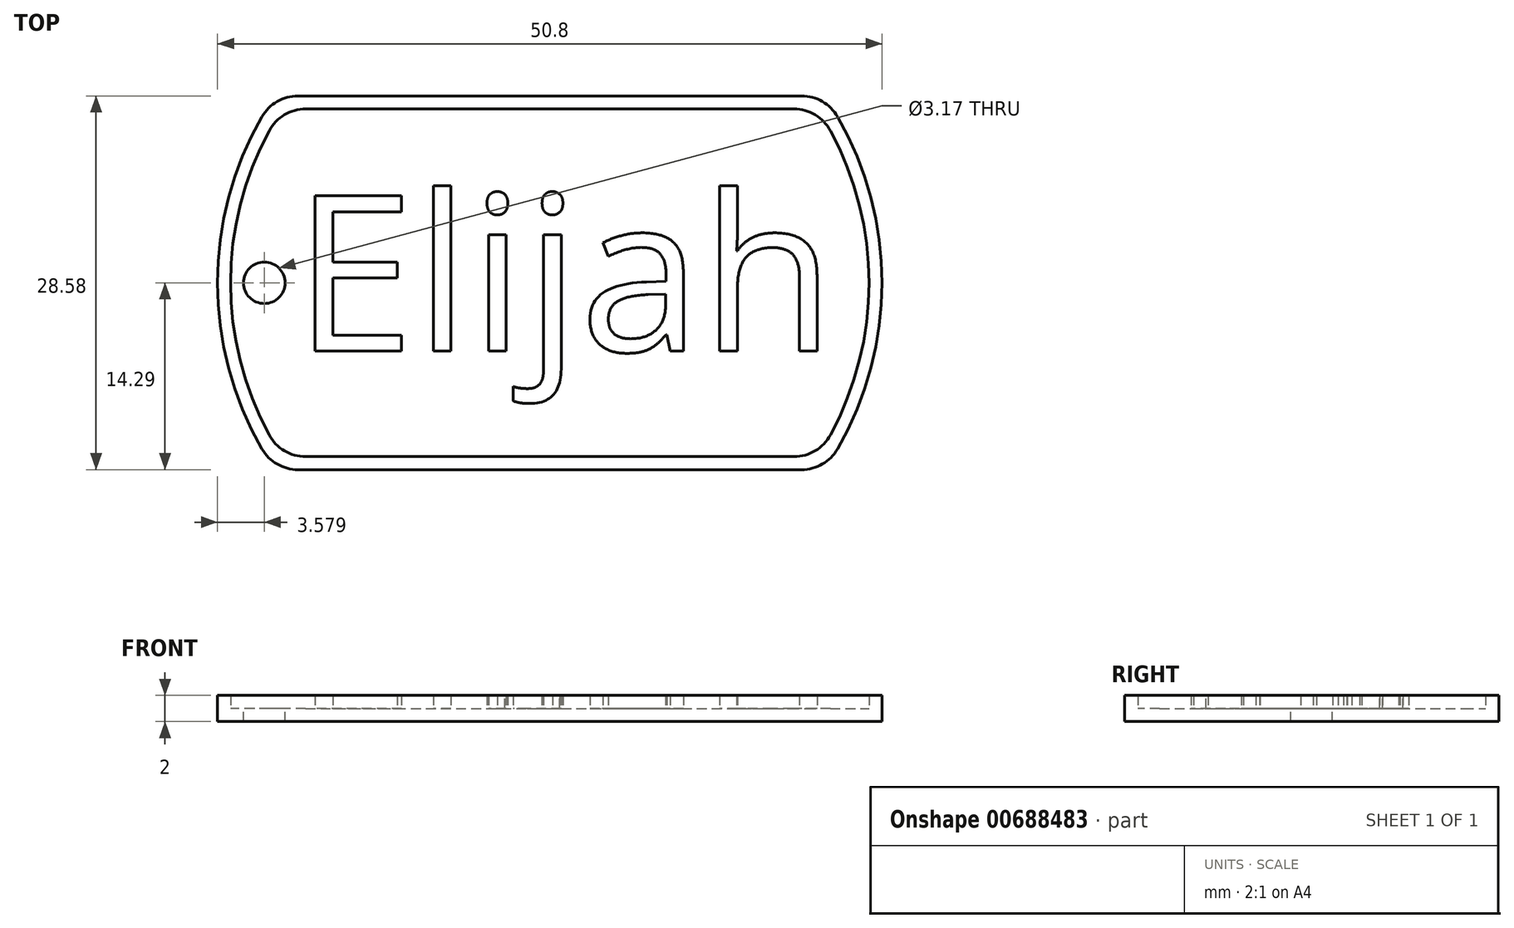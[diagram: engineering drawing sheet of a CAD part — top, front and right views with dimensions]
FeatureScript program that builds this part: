
annotation { "Feature Type Name" : "Feature", "Feature Type Description" : "" }
export const myFeature = defineFeature(function(context is Context, id is Id, definition is map)
    precondition{}
    {
        {
            var Q0;
            Q0=qCreatedBy(makeId("Top.planeOp"),FACE);
            var sketch = newSketch(context, id + "F0", { "sketchPlane" : qUnion([Q0])});
            skArc(sketch, "E0", {"start": v(-22, 12.7) * mm, "mid": v(-25.4, 0) * mm, "end": v(-22, -12.7) * mm});
            skLineSegment(sketch, "E1.top", {"start": v(-19.25, -14.29) * mm, "end": v(19.25, -14.29) * mm});
            skArc(sketch, "E2.trimOffspring", {"start": v(22, -12.7) * mm, "mid": v(25.4, 0) * mm, "end": v(22, 12.7) * mm});
            skLineSegment(sketch, "E3", {"start": v(-19.25, 14.29) * mm, "end": v(19.25, 14.29) * mm});
            skPoint(sketch, "E4.visualSharp", {"position": v(-21, 14.29) * mm});
            skArc(sketch, "E4.filletArc", {"start": v(-19.25, 14.29) * mm, "mid": v(-20.83, 13.86) * mm, "end": v(-22, 12.7) * mm});
            skPoint(sketch, "E5.visualSharp", {"position": v(21, 14.29) * mm});
            skArc(sketch, "E5.filletArc", {"start": v(22, 12.7) * mm, "mid": v(20.83, 13.86) * mm, "end": v(19.25, 14.29) * mm});
            skPoint(sketch, "E6.visualSharp", {"position": v(21, -14.29) * mm});
            skArc(sketch, "E6.filletArc", {"start": v(19.25, -14.29) * mm, "mid": v(20.83, -13.86) * mm, "end": v(22, -12.7) * mm});
            skPoint(sketch, "E7.visualSharp", {"position": v(-21, -14.29) * mm});
            skArc(sketch, "E7.filletArc", {"start": v(-22, -12.7) * mm, "mid": v(-20.83, -13.86) * mm, "end": v(-19.25, -14.29) * mm});
            skSolve(sketch);
        }
        {
            var Q0;
            Q0=makeQuery(id+"F0.imprint","IMPRINT",FACE,{"disambiguationData":[TD([[makeQuery(id+"F0.imprint","IMPRINT",EDGE,{"derivedFrom":sQuery(id+"F0.wireOp",EDGE,"E0")}),1.0]])]});
            extrude(context, id + "F1", {"entities" : qUnion([Q0]), "depth" : 1 * mm, "offsetDistance" : 25.4 * mm});
        }
        {
            var Q0;
            Q0=makeQuery(id+"F1.opExtrude","CAP_FACE",FACE,{"disambiguationData":[OSD([sQuery(id+"F0.wireOp",EDGE,"E0"),sQuery(id+"F0.wireOp",EDGE,"E1.top"),sQuery(id+"F0.wireOp",EDGE,"E2.trimOffspring"),sQuery(id+"F0.wireOp",EDGE,"E3"),sQuery(id+"F0.wireOp",EDGE,"E4.filletArc"),sQuery(id+"F0.wireOp",EDGE,"E5.filletArc"),sQuery(id+"F0.wireOp",EDGE,"E6.filletArc"),sQuery(id+"F0.wireOp",EDGE,"E7.filletArc")])],"isStart":false});
            var sketch = newSketch(context, id + "F2", { "sketchPlane" : qUnion([Q0])});
            skLineSegment(sketch, "E8.0", {"start": v(-18.66, 13.29) * mm, "end": v(18.66, 13.29) * mm});
            skArc(sketch, "E8.1", {"start": v(-21.45, 11.63) * mm, "mid": v(-24.4, 0) * mm, "end": v(-21.45, -11.63) * mm});
            skLineSegment(sketch, "E8.2", {"start": v(-18.66, -13.29) * mm, "end": v(18.66, -13.29) * mm});
            skArc(sketch, "E8.3", {"start": v(21.45, -11.63) * mm, "mid": v(24.4, 0) * mm, "end": v(21.45, 11.63) * mm});
            skPoint(sketch, "E9.visualSharp", {"position": v(-20.46, 13.29) * mm});
            skArc(sketch, "E9.filletArc", {"start": v(-18.66, 13.29) * mm, "mid": v(-20.29, 12.84) * mm, "end": v(-21.45, 11.63) * mm});
            skPoint(sketch, "E10.visualSharp", {"position": v(20.46, 13.29) * mm});
            skArc(sketch, "E10.filletArc", {"start": v(21.45, 11.63) * mm, "mid": v(20.29, 12.84) * mm, "end": v(18.66, 13.29) * mm});
            skPoint(sketch, "E11.visualSharp", {"position": v(20.46, -13.29) * mm});
            skArc(sketch, "E11.filletArc", {"start": v(18.66, -13.29) * mm, "mid": v(20.29, -12.84) * mm, "end": v(21.45, -11.63) * mm});
            skPoint(sketch, "E12.visualSharp", {"position": v(-20.46, -13.29) * mm});
            skArc(sketch, "E12.filletArc", {"start": v(-21.45, -11.63) * mm, "mid": v(-20.29, -12.84) * mm, "end": v(-18.66, -13.29) * mm});
            skLineSegment(sketch, "E13.0", {"start": v(-19.25, 14.29) * mm, "end": v(19.25, 14.29) * mm});
            skArc(sketch, "E13.1", {"start": v(-22, 12.7) * mm, "mid": v(-25.4, 0) * mm, "end": v(-22, -12.7) * mm});
            skLineSegment(sketch, "E13.2", {"start": v(-19.25, -14.29) * mm, "end": v(19.25, -14.29) * mm});
            skArc(sketch, "E13.3", {"start": v(22, -12.7) * mm, "mid": v(25.4, 0) * mm, "end": v(22, 12.7) * mm});
            skPoint(sketch, "E14.visualSharp", {"position": v(-21, -14.29) * mm});
            skArc(sketch, "E14.filletArc", {"start": v(-22, -12.7) * mm, "mid": v(-20.83, -13.86) * mm, "end": v(-19.25, -14.29) * mm});
            skPoint(sketch, "E15.visualSharp", {"position": v(21, -14.29) * mm});
            skArc(sketch, "E15.filletArc", {"start": v(19.25, -14.29) * mm, "mid": v(20.83, -13.86) * mm, "end": v(22, -12.7) * mm});
            skPoint(sketch, "E16.visualSharp", {"position": v(21, 14.29) * mm});
            skArc(sketch, "E16.filletArc", {"start": v(22, 12.7) * mm, "mid": v(20.83, 13.86) * mm, "end": v(19.25, 14.29) * mm});
            skPoint(sketch, "E17.visualSharp", {"position": v(-21, 14.29) * mm});
            skArc(sketch, "E17.filletArc", {"start": v(-19.25, 14.29) * mm, "mid": v(-20.83, 13.86) * mm, "end": v(-22, 12.7) * mm});
            skSolve(sketch);
        }
        {
            var Q0;
            Q0=makeQuery(id+"F2.imprint","IMPRINT",FACE,{"disambiguationData":[TD([[makeQuery(id+"F2.imprint","IMPRINT",EDGE,{"derivedFrom":sQuery(id+"F2.wireOp",EDGE,"E8.0")}),1.0]])]});
            extrude(context, id + "F3", {"entities" : qUnion([Q0]), "operationType" : NewBodyOperationType.ADD, "depth" : 1 * mm, "offsetDistance" : 25.4 * mm});
        }
        {
            var Q0;
            Q0=makeQuery(id+"F1.opExtrude","CAP_FACE",FACE,{"disambiguationData":[OSD([sQuery(id+"F0.wireOp",EDGE,"E0"),sQuery(id+"F0.wireOp",EDGE,"E1.top"),sQuery(id+"F0.wireOp",EDGE,"E2.trimOffspring"),sQuery(id+"F0.wireOp",EDGE,"E3"),sQuery(id+"F0.wireOp",EDGE,"E4.filletArc"),sQuery(id+"F0.wireOp",EDGE,"E5.filletArc"),sQuery(id+"F0.wireOp",EDGE,"E6.filletArc"),sQuery(id+"F0.wireOp",EDGE,"E7.filletArc")])],"isStart":false});
            var sketch = newSketch(context, id + "F4", { "sketchPlane" : qUnion([Q0])});
            skCircle(sketch, "E18", {"center": v(-21.82, 0) * mm, "radius": 1.59 * mm});
            skSolve(sketch);
        }
        {
            var Q0;
            Q0=makeQuery(id+"F4.imprint","IMPRINT",FACE,{"disambiguationData":[TD([[makeQuery(id+"F4.imprint","IMPRINT",EDGE,{"derivedFrom":sQuery(id+"F4.wireOp",EDGE,"E18")}),1.0]])]});
            extrude(context, id + "F5", {"entities" : qUnion([Q0]), "operationType" : NewBodyOperationType.REMOVE, "oppositeDirection" : true, "depth" : 1 * mm, "offsetDistance" : 25.4 * mm});
        }
        {
            var Q0;
            Q0=makeQuery(id+"F2.imprint","IMPRINT",FACE,{"disambiguationData":[TD([[makeQuery(id+"F2.imprint","IMPRINT",EDGE,{"derivedFrom":sQuery(id+"F2.wireOp",EDGE,"E8.0")}),-1.0]])]});
            var sketch = newSketch(context, id + "F6", { "sketchPlane" : qUnion([Q0])});
            skText(sketch, "E19", { "text": "Elijah", "fontName": "OpenSans-Regular.ttf"});
            const initialGuessF6  = {"E19": [-0.01958, -0.00523, 1, 0, 0.01198]};
            skSetInitialGuess(sketch, initialGuessF6);
            skSolve(sketch);
        }
        {
            var Q0;
            Q0 = qSketchRegion(id + "F6", true);
            extrude(context, id + "F7", {"entities" : qUnion([Q0]), "operationType" : NewBodyOperationType.ADD, "depth" : 1 * mm, "offsetDistance" : 25.4 * mm});
        }
    });
